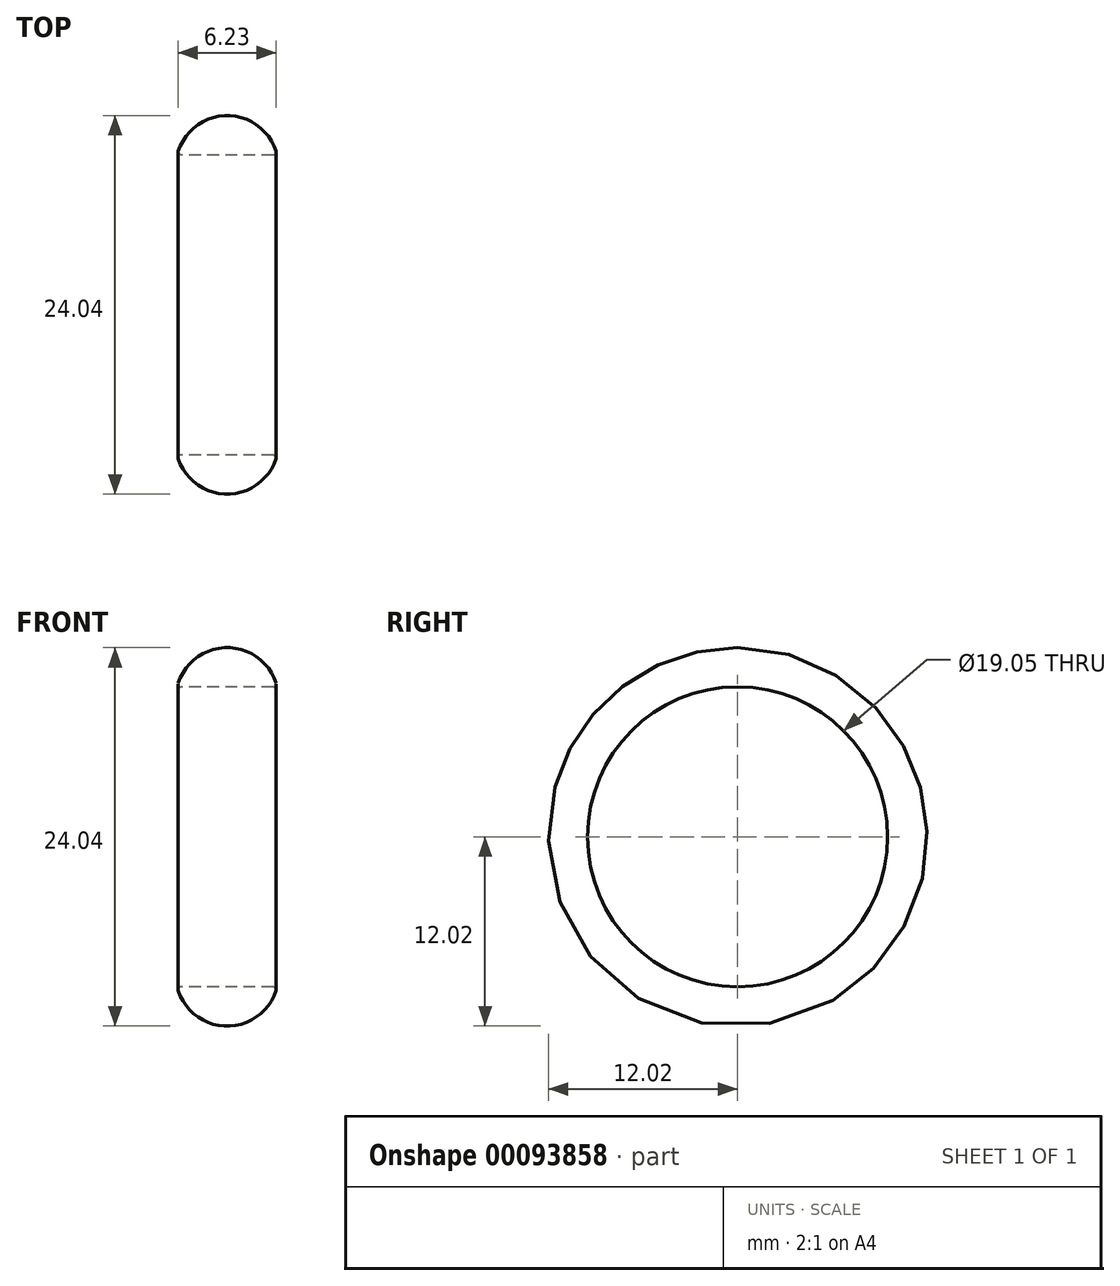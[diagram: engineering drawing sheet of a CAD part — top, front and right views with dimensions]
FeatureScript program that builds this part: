
annotation { "Feature Type Name" : "Feature", "Feature Type Description" : "" }
export const myFeature = defineFeature(function(context is Context, id is Id, definition is map)
    precondition{}
    {
        {
            var Q0;
            Q0=qCreatedBy(makeId("Front.planeOp"),FACE);
            var sketch = newSketch(context, id + "F0", { "sketchPlane" : qUnion([Q0])});
            skLineSegment(sketch, "E0", {"start": v(0, 0) * mm, "end": v(0, 9.52) * mm});
            skLineSegment(sketch, "E1", {"start": v(0.24, 9.52) * mm, "end": v(6.1, 9.52) * mm});
            skArc(sketch, "E2", {"start": v(6.28, 9.76) * mm, "mid": v(3.17, 12.02) * mm, "end": v(0.07, 9.76) * mm});
            skPoint(sketch, "E3.visualSharp", {"position": v(0, 9.52) * mm});
            skArc(sketch, "E3.filletArc", {"start": v(0.07, 9.76) * mm, "mid": v(0.1, 9.6) * mm, "end": v(0.24, 9.52) * mm});
            skPoint(sketch, "E4.visualSharp", {"position": v(6.35, 9.52) * mm});
            skArc(sketch, "E4.filletArc", {"start": v(6.1, 9.52) * mm, "mid": v(6.26, 9.6) * mm, "end": v(6.28, 9.76) * mm});
            skLineSegment(sketch, "E5", {"start": v(0, 0) * mm, "end": v(4.1, 0) * mm});
            skSolve(sketch);
        }
        {
            var Q0;
            Q0=makeQuery(id+"F0.imprint","IMPRINT",FACE,{"disambiguationData":[TD([[makeQuery(id+"F0.imprint","IMPRINT",EDGE,{"derivedFrom":sQuery(id+"F0.wireOp",EDGE,"E1")}),1.0]])]});
            var Q1;
            Q1=sQuery(id+"F0.wireOp",EDGE,"E5");
            revolve(context, id + "F1", {"entities" : qUnion([Q0]), "axis" : qUnion([Q1]), "revolveType" : RevolveType.FULL});
        }
    });
